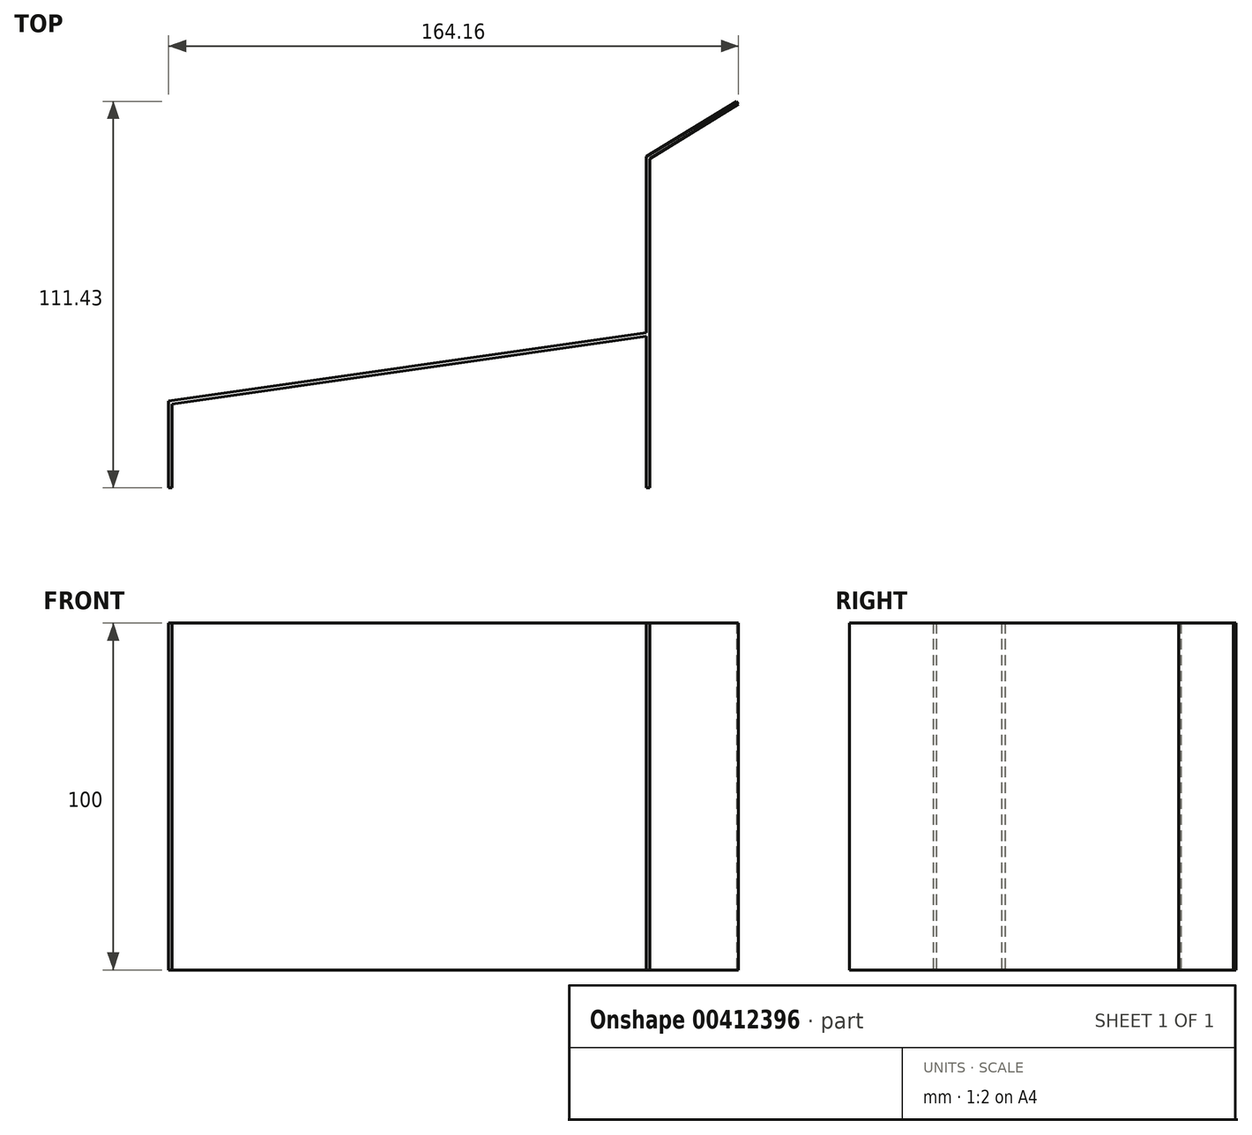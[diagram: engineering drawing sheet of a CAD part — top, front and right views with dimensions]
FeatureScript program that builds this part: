
annotation { "Feature Type Name" : "Feature", "Feature Type Description" : "" }
export const myFeature = defineFeature(function(context is Context, id is Id, definition is map)
    precondition{}
    {
        {
            var Q0;
            Q0=qCreatedBy(makeId("Top.planeOp"),FACE);
            var sketch = newSketch(context, id + "F0", { "sketchPlane" : qUnion([Q0])});
            skLineSegment(sketch, "E0", {"start": v(-72.78, -27.2) * mm, "end": v(-72.78, -2.2) * mm});
            skLineSegment(sketch, "E1", {"start": v(-72.78, -2.2) * mm, "end": v(64.8, 17.58) * mm});
            skLineSegment(sketch, "E2", {"start": v(65.8, 17.72) * mm, "end": v(65.8, 67.72) * mm});
            skLineSegment(sketch, "E3", {"start": v(65.8, 67.72) * mm, "end": v(91.38, 83.39) * mm});
            skLineSegment(sketch, "E4", {"start": v(65.8, 17.72) * mm, "end": v(65.8, -27.2) * mm});
            skLineSegment(sketch, "E5.0", {"start": v(64.8, 16.57) * mm, "end": v(64.8, -27.2) * mm});
            skLineSegment(sketch, "E5.1", {"start": v(-71.78, -3.06) * mm, "end": v(64.8, 16.57) * mm});
            skLineSegment(sketch, "E5.2", {"start": v(-71.78, -27.2) * mm, "end": v(-71.78, -3.06) * mm});
            skLineSegment(sketch, "E6", {"start": v(-71.78, -27.2) * mm, "end": v(-72.78, -27.2) * mm});
            skLineSegment(sketch, "E7", {"start": v(65.8, -27.2) * mm, "end": v(64.8, -27.2) * mm});
            skLineSegment(sketch, "E8.0", {"start": v(64.8, 68.28) * mm, "end": v(90.86, 84.24) * mm});
            skLineSegment(sketch, "E8.1", {"start": v(64.8, 17.58) * mm, "end": v(64.8, 68.28) * mm});
            skLineSegment(sketch, "E9", {"start": v(90.86, 84.24) * mm, "end": v(91.38, 83.39) * mm});
            skSolve(sketch);
        }
        {
            var Q0;
            Q0 = qSketchRegion(id + "F0", true);
            extrude(context, id + "F1", {"entities" : qUnion([Q0]), "depth" : 100 * mm});
        }
    });
